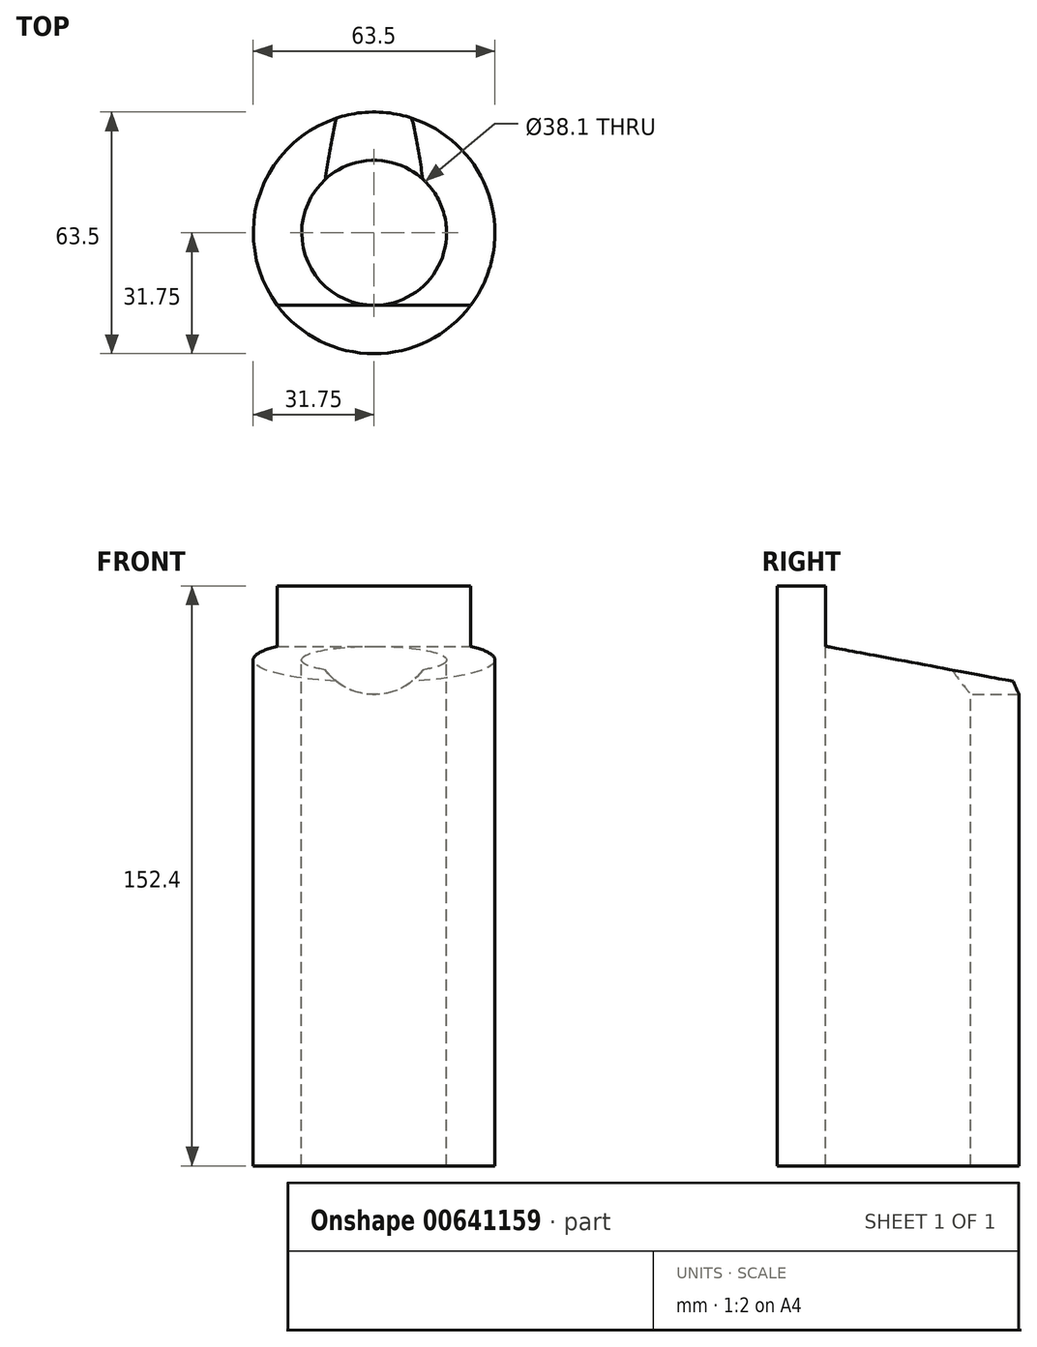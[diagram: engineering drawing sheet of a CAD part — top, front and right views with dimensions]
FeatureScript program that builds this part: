
annotation { "Feature Type Name" : "Feature", "Feature Type Description" : "" }
export const myFeature = defineFeature(function(context is Context, id is Id, definition is map)
    precondition{}
    {
        {
            var Q0;
            Q0=qCreatedBy(makeId("Top.planeOp"),FACE);
            var sketch = newSketch(context, id + "F0", { "sketchPlane" : qUnion([Q0])});
            skCircle(sketch, "E0", {"center": v(0, 0) * mm, "radius": 19.05 * mm});
            skCircle(sketch, "E1", {"center": v(0, 0) * mm, "radius": 31.75 * mm});
            skSolve(sketch);
        }
        {
            var Q0;
            Q0=makeQuery(id+"F0.imprint","IMPRINT",FACE,{"disambiguationData":[TD([[makeQuery(id+"F0.imprint","IMPRINT",EDGE,{"derivedFrom":sQuery(id+"F0.wireOp",EDGE,"E0")}),-1.0]])]});
            extrude(context, id + "F1", {"entities" : qUnion([Q0]), "oppositeDirection" : true, "depth" : 152.4 * mm, "offsetDistance" : 25.4 * mm});
        }
        {
            var Q0;
            Q0=qCreatedBy(makeId("Right.planeOp"),FACE);
            var sketch = newSketch(context, id + "F2", { "sketchPlane" : qUnion([Q0])});
            skLineSegment(sketch, "E2", {"start": v(-19.05, 0) * mm, "end": v(-19.05, -15.88) * mm});
            skLineSegment(sketch, "E3", {"start": v(31.75, 0) * mm, "end": v(31.75, -25.4) * mm});
            skPoint(sketch, "E4.third.point", {"position": v(55.24, -25.4) * mm});
            skLineSegment(sketch, "E5", {"start": v(31.75, 0) * mm, "end": v(-19.05, 0) * mm});
            skLineSegment(sketch, "E6", {"start": v(31.75, -25.4) * mm, "end": v(-19.05, -15.88) * mm});
            skSolve(sketch);
        }
        {
            var Q0;
            Q0 = qSketchRegion(id + "F2", true);
            extrude(context, id + "F3", {"entities" : qUnion([Q0]), "operationType" : NewBodyOperationType.REMOVE, "endBound" : BoundingType.SYMMETRIC, "oppositeDirection" : true, "depth" : 101.6 * mm, "offsetDistance" : 25.4 * mm});
        }
        {
            var Q0;
            Q0=qCreatedBy(makeId("Front.planeOp"),FACE);
            var sketch = newSketch(context, id + "F4", { "sketchPlane" : qUnion([Q0])});
            skCircle(sketch, "E7", {"center": v(0, -12.7) * mm, "radius": 15.88 * mm});
            skSolve(sketch);
        }
        {
            var Q0;
            Q0 = qSketchRegion(id + "F4", true);
            extrude(context, id + "F5", {"entities" : qUnion([Q0]), "operationType" : NewBodyOperationType.REMOVE, "oppositeDirection" : true, "depth" : 50.8 * mm, "offsetDistance" : 25.4 * mm});
        }
        {
            var Q0;
            Q0=qCreatedBy(makeId("Front.planeOp"),FACE);
            cPlane(context, id + "F6", {"entities" : qUnion([Q0]), "cplaneType" : CPlaneType.OFFSET, "offset" : 19.05 * mm, "width" : 152.4 * mm, "height" : 152.4 * mm});
        }
    });
